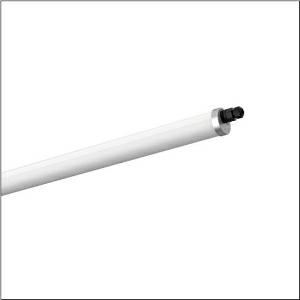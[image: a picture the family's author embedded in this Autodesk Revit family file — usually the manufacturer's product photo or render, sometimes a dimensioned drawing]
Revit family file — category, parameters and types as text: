
# Revit family: monsun_r__31_tube_51ft10dn480a_9fe9
name_source: partatom
category: Lighting Fixtures
units: mm (PartAtom-declared; Revit-internal decimal feet)

## family parameters
Cut with Voids When Loaded = No
Host = Face
Light Source = No
Part Type = Normal
Room Calculation Point = No
Round Connector Dimension = Use Diameter
Shared = No

## types (1)
- Monsun® 31 Tube (1 x LED, 8000 lm, 50 W, 4000K)
    Apparent Load = 50 VA
    CIE Flux Codes = 42 71 89 91 100
    Color Rendering = 80
    Color Temperature = 4000K
    Default Elevation = 1800 mm
    Description = Monsun® 31 Tube, tubular luminaire, primary optical cover: diffuser, of PMMA, light emission: direct distribution, primary light characteristic: symmetric, installation type: suspended mounting, surface-mounted, LED, rated luminous flux: 8.000lm, luminous efficacy: 160lm/W, light colour: 840, colour temperature: 4000K, with with 1 terminal, 5-pole, max. 2.5mm², through-wiring: 5x 1.5mm², mains connection: 220..240V, AC, 50/60Hz, rated input power: 50W, housing, cylindrical, of PMMA, semi-transparent, matt white, length: 1.570mm, diameter: 75mm, end cap, of stainless steel (V2A), protection rating (complete): IP67/IP69K, insulation class (complete): insulation class I (protective earthing), certification: CE, UKCA, impact resistance: IK07, permissible operating ambient temperature: -20..+40°C, corresponds to IFS (International Featured Standards) requirements for safety and quality in the food industry, packaging unit: 1 piece
    Height = 83 mm
    Lamp = 1 x LED
    Lamp Light Flux = 8000 lm
    Lamp Power = 50 W
    Lamp count = 1
    Length = 1570 mm
    Luminous efficacy = 160 lm/W
    Manufacturer = Siteco
    ModVariant = No
    Model = 51FT10DN480A
    Mounting Place = Ceiling
    Mounting Type = Pendant
    Number of Poles = 1
    OnlyDefault = Yes
    Power Factor = 1
    Product Name = Monsun® 31 Tube
    Product group = tubular luminaire
    ProductGroupID = 907
    Protection Class = Protection class I
    RLX_Detail_Level = 1
    RlxData = <blob elided: 24793 chars, md5=0c6ed229>
    Socket = socket
    Standby Power = 0 W
    System Light Flux = 8000 lm
    System Power = 50 W
    Type Comments = Product without accessories
    Type Image = l_1228461.jpg
    URL = http://relux.com
    VarID = ---
    Voltage = 0 V
    Weight = 0.00 kg
    Width = 75 mm

## geometry (parser evidence)
native form markers: Blend x4, Sweep x12
no freeform markers — native parametric forms only
